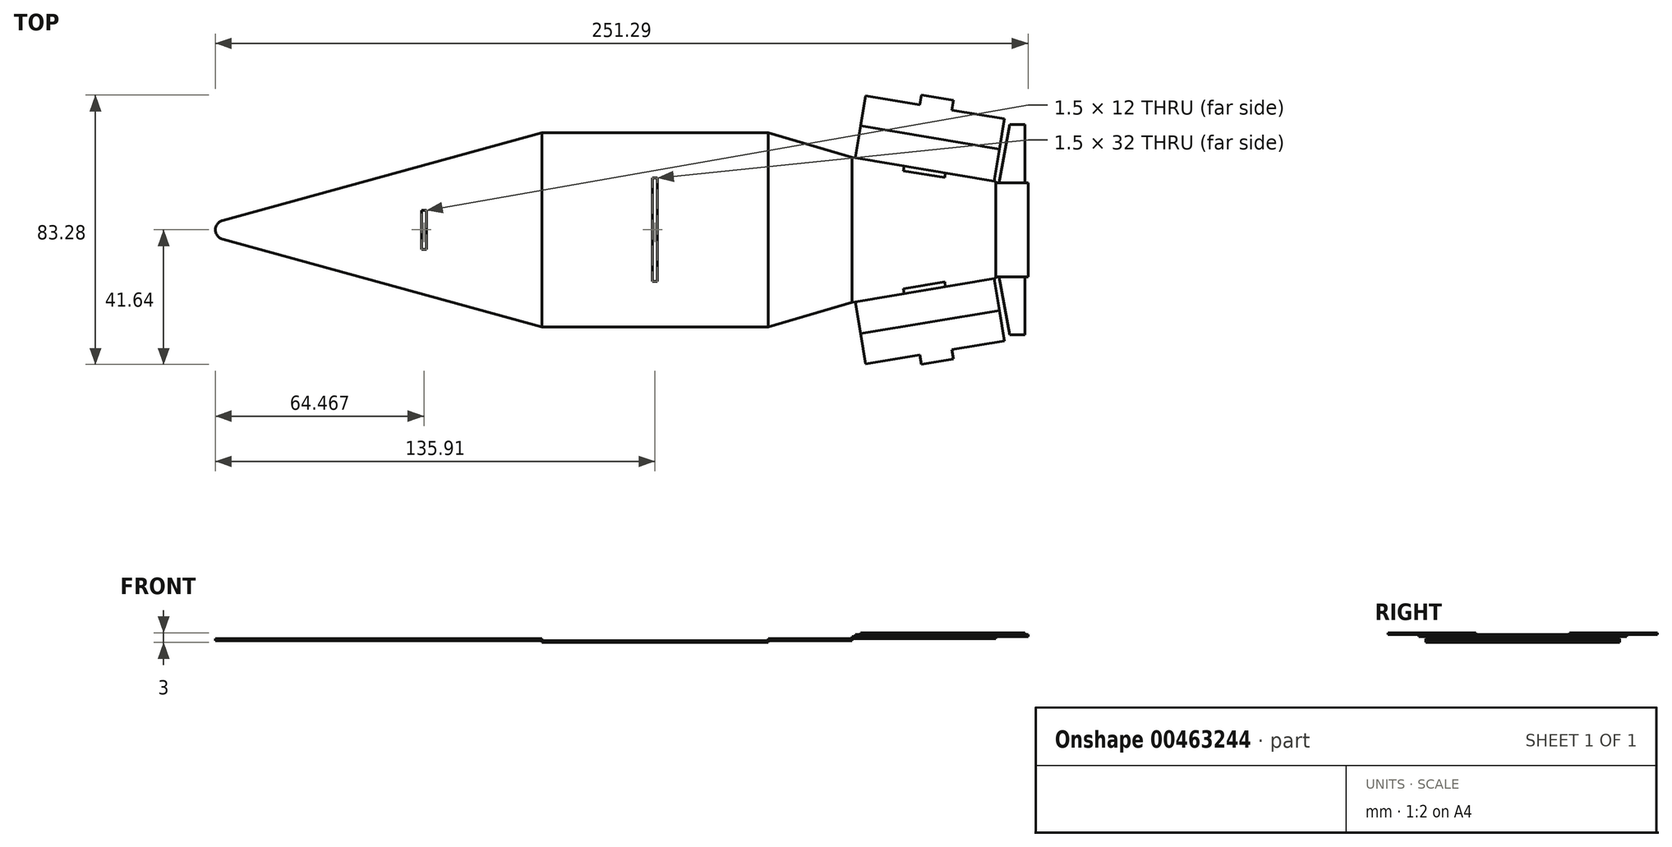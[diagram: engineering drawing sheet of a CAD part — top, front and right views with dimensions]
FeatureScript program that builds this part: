
annotation { "Feature Type Name" : "Feature", "Feature Type Description" : "" }
export const myFeature = defineFeature(function(context is Context, id is Id, definition is map)
    precondition{}
    {
        {
            var Q0;
            Q0=qCreatedBy(makeId("Top.planeOp"),FACE);
            var sketch = newSketch(context, id + "F0", { "sketchPlane" : qUnion([Q0])});
            skLineSegment(sketch, "E0.bottom", {"start": v(-35, 30) * mm, "end": v(35, 30) * mm});
            skLineSegment(sketch, "E0.top", {"start": v(-35, -30) * mm, "end": v(35, -30) * mm});
            skLineSegment(sketch, "E0.left", {"start": v(-35, 30) * mm, "end": v(-35, -30) * mm});
            skLineSegment(sketch, "E0.right", {"start": v(35, 30) * mm, "end": v(35, -30) * mm});
            skPoint(sketch, "E0.middle", {"position": v(0, 0) * mm});
            skLineSegment(sketch, "E1.0", {"start": v(-0.75, 16) * mm, "end": v(-0.75, -16) * mm});
            skLineSegment(sketch, "E2.0", {"start": v(0.75, 16) * mm, "end": v(0.75, -16) * mm});
            skLineSegment(sketch, "E3.0", {"start": v(-0.75, -16) * mm, "end": v(0.75, -16) * mm});
            skLineSegment(sketch, "E4.0", {"start": v(-0.75, 16) * mm, "end": v(0.75, 16) * mm});
            skSolve(sketch);
        }
        {
            var Q0;
            Q0 = qSketchRegion(id + "F0", true);
            extrude(context, id + "F1", {"entities" : qUnion([Q0]), "depth" : .6 * mm});
        }
        {
            var Q0;
            Q0=makeQuery(id+"F1.opExtrude","CAP_FACE",FACE,{"disambiguationData":[OSD([sQuery(id+"F0.wireOp",EDGE,"E0.bottom"),sQuery(id+"F0.wireOp",EDGE,"E0.top"),sQuery(id+"F0.wireOp",EDGE,"E0.left"),sQuery(id+"F0.wireOp",EDGE,"E0.right"),sQuery(id+"F0.wireOp",EDGE,"E1.0"),sQuery(id+"F0.wireOp",EDGE,"E2.0"),sQuery(id+"F0.wireOp",EDGE,"E3.0"),sQuery(id+"F0.wireOp",EDGE,"E4.0")])],"isStart":false});
            var sketch = newSketch(context, id + "F2", { "sketchPlane" : qUnion([Q0])});
            skLineSegment(sketch, "E5", {"start": v(-144.24, 0) * mm, "end": v(-35, 30) * mm});
            skLineSegment(sketch, "E6", {"start": v(-35, 30) * mm, "end": v(-35, -30) * mm});
            skLineSegment(sketch, "E7", {"start": v(-35, -30) * mm, "end": v(-144.24, 0) * mm});
            skLineSegment(sketch, "E8", {"start": v(-70.7, 6) * mm, "end": v(-70.7, -6) * mm});
            skLineSegment(sketch, "E9.0", {"start": v(-72.2, 6) * mm, "end": v(-72.2, -6) * mm});
            skLineSegment(sketch, "E10", {"start": v(-72.2, 6) * mm, "end": v(-70.7, 6) * mm});
            skLineSegment(sketch, "E11", {"start": v(-72.2, -6) * mm, "end": v(-70.7, -6) * mm});
            skSolve(sketch);
        }
        {
            var Q0;
            Q0 = qSketchRegion(id + "F2", true);
            extrude(context, id + "F3", {"entities" : qUnion([Q0]), "depth" : .6 * mm});
        }
        {
            var Q0;
            Q0=makeQuery(id+"F1.opExtrude","CAP_FACE",FACE,{"disambiguationData":[OSD([sQuery(id+"F0.wireOp",EDGE,"E0.bottom"),sQuery(id+"F0.wireOp",EDGE,"E0.top"),sQuery(id+"F0.wireOp",EDGE,"E0.left"),sQuery(id+"F0.wireOp",EDGE,"E0.right"),sQuery(id+"F0.wireOp",EDGE,"E1.0"),sQuery(id+"F0.wireOp",EDGE,"E2.0"),sQuery(id+"F0.wireOp",EDGE,"E3.0"),sQuery(id+"F0.wireOp",EDGE,"E4.0")])],"isStart":false});
            var sketch = newSketch(context, id + "F4", { "sketchPlane" : qUnion([Q0])});
            skLineSegment(sketch, "E12.0", {"start": v(35, 30) * mm, "end": v(35, -30) * mm});
            skLineSegment(sketch, "E13", {"start": v(35, 30) * mm, "end": v(60.94, 22.41) * mm});
            skLineSegment(sketch, "E14.MirrorCS", {"start": v(35, -30) * mm, "end": v(60.94, -22.41) * mm});
            skLineSegment(sketch, "E15", {"start": v(60.94, 22.41) * mm, "end": v(60.94, -22.41) * mm});
            skSolve(sketch);
        }
        {
            var Q0;
            Q0 = qSketchRegion(id + "F4", true);
            extrude(context, id + "F5", {"entities" : qUnion([Q0]), "depth" : .6 * mm});
        }
        {
            var Q0;
            Q0=makeQuery(id+"F5.opExtrude","CAP_FACE",FACE,{"disambiguationData":[OSD([sQuery(id+"F4.wireOp",EDGE,"E12.0"),sQuery(id+"F4.wireOp",EDGE,"E13"),sQuery(id+"F4.wireOp",EDGE,"E14.MirrorCS"),sQuery(id+"F4.wireOp",EDGE,"E15")])],"isStart":false});
            var sketch = newSketch(context, id + "F6", { "sketchPlane" : qUnion([Q0])});
            skLineSegment(sketch, "E16.0", {"start": v(60.94, 22.41) * mm, "end": v(60.94, -22.41) * mm});
            skLineSegment(sketch, "E17", {"start": v(60.94, 22.41) * mm, "end": v(105.38, 15) * mm});
            skPoint(sketch, "E18.endSnap0", {"position": v(60.94, 0) * mm});
            skLineSegment(sketch, "E19.MirrorCS", {"start": v(60.94, -22.41) * mm, "end": v(105.38, -15) * mm});
            skLineSegment(sketch, "E20", {"start": v(105.38, 15) * mm, "end": v(105.38, -15) * mm});
            skSolve(sketch);
        }
        {
            var Q0;
            Q0 = qSketchRegion(id + "F6", true);
            extrude(context, id + "F7", {"entities" : qUnion([Q0]), "depth" : .6 * mm});
        }
        {
            var Q0;
            Q0=makeQuery(id+"F7.opExtrude","CAP_FACE",FACE,{"disambiguationData":[OSD([sQuery(id+"F6.wireOp",EDGE,"E16.0"),sQuery(id+"F6.wireOp",EDGE,"E17"),sQuery(id+"F6.wireOp",EDGE,"E19.MirrorCS"),sQuery(id+"F6.wireOp",EDGE,"E20")])],"isStart":false});
            var sketch = newSketch(context, id + "F8", { "sketchPlane" : qUnion([Q0])});
            skLineSegment(sketch, "E21.0", {"start": v(61.93, -22.25) * mm, "end": v(105.38, -15) * mm});
            skLineSegment(sketch, "E22", {"start": v(105.38, -15) * mm, "end": v(107.02, -24.87) * mm});
            skLineSegment(sketch, "E23", {"start": v(63.57, -32.11) * mm, "end": v(107.02, -24.87) * mm});
            skLineSegment(sketch, "E24.0", {"start": v(61.93, -22.25) * mm, "end": v(63.57, -32.11) * mm});
            skPoint(sketch, "E25.orphan", {"position": v(60.94, -22.41) * mm});
            skPoint(sketch, "E26.endSnap0", {"position": v(105.38, 0) * mm});
            skLineSegment(sketch, "E27.MirrorCS", {"start": v(105.38, 15) * mm, "end": v(107.02, 24.87) * mm});
            skLineSegment(sketch, "E28.MirrorCS", {"start": v(61.93, 22.25) * mm, "end": v(105.38, 15) * mm});
            skLineSegment(sketch, "E29.MirrorCS", {"start": v(63.57, 32.11) * mm, "end": v(107.02, 24.87) * mm});
            skLineSegment(sketch, "E30.MirrorCS", {"start": v(61.93, 22.25) * mm, "end": v(63.57, 32.11) * mm});
            skPoint(sketch, "E31.MirrorP", {"position": v(60.94, 22.41) * mm});
            skLineSegment(sketch, "E32.0", {"start": v(105.38, 14.5) * mm, "end": v(105.38, -14.5) * mm});
            skLineSegment(sketch, "E33.0", {"start": v(115.38, 14.5) * mm, "end": v(115.38, -14.5) * mm});
            skLineSegment(sketch, "E34.0", {"start": v(105.38, 14.5) * mm, "end": v(115.38, 14.5) * mm});
            skLineSegment(sketch, "E35.0", {"start": v(105.38, -14.5) * mm, "end": v(115.38, -14.5) * mm});
            skPoint(sketch, "E36.orphan", {"position": v(105.38, 15) * mm});
            skSolve(sketch);
        }
        {
            var Q0;
            Q0 = qSketchRegion(id + "F8", true);
            extrude(context, id + "F9", {"entities" : qUnion([Q0]), "depth" : .6 * mm});
        }
        {
            var Q0;
            Q0=makeQuery(id+"F9.opExtrude","CAP_FACE",FACE,{"disambiguationData":[OSD([sQuery(id+"F8.wireOp",EDGE,"E21.0"),sQuery(id+"F8.wireOp",EDGE,"E22"),sQuery(id+"F8.wireOp",EDGE,"E23"),sQuery(id+"F8.wireOp",EDGE,"E24.0")])],"isStart":false});
            var sketch = newSketch(context, id + "F10", { "sketchPlane" : qUnion([Q0])});
            skLineSegment(sketch, "E37.0", {"start": v(63.57, -32.11) * mm, "end": v(107.02, -24.87) * mm});
            skLineSegment(sketch, "E38.0", {"start": v(65.14, -41.48) * mm, "end": v(81.93, -38.69) * mm});
            skLineSegment(sketch, "E39", {"start": v(63.57, -32.11) * mm, "end": v(65.14, -41.48) * mm});
            skLineSegment(sketch, "E40", {"start": v(107.02, -24.87) * mm, "end": v(108.59, -34.24) * mm});
            skLineSegment(sketch, "E41.0", {"start": v(82.42, -41.64) * mm, "end": v(92.29, -40) * mm});
            skLineSegment(sketch, "E42.0", {"start": v(92.29, -40) * mm, "end": v(91.8, -37.04) * mm});
            skLineSegment(sketch, "E43.0", {"start": v(82.42, -41.64) * mm, "end": v(81.93, -38.69) * mm});
            skLineSegment(sketch, "E44.trimOffspring", {"start": v(91.8, -37.04) * mm, "end": v(108.59, -34.24) * mm});
            skLineSegment(sketch, "E45.MirrorCS", {"start": v(92.29, 40) * mm, "end": v(91.8, 37.04) * mm});
            skLineSegment(sketch, "E46.MirrorCS", {"start": v(82.42, 41.64) * mm, "end": v(81.93, 38.69) * mm});
            skLineSegment(sketch, "E47.MirrorCS", {"start": v(63.57, 32.11) * mm, "end": v(107.02, 24.87) * mm});
            skLineSegment(sketch, "E48.MirrorCS", {"start": v(65.14, 41.48) * mm, "end": v(81.93, 38.69) * mm});
            skLineSegment(sketch, "E49.MirrorCS", {"start": v(91.8, 37.04) * mm, "end": v(108.59, 34.24) * mm});
            skLineSegment(sketch, "E50.MirrorCS", {"start": v(63.57, 32.11) * mm, "end": v(65.14, 41.48) * mm});
            skLineSegment(sketch, "E51.MirrorCS", {"start": v(82.42, 41.64) * mm, "end": v(92.29, 40) * mm});
            skLineSegment(sketch, "E52.MirrorCS", {"start": v(107.02, 24.87) * mm, "end": v(108.59, 34.24) * mm});
            skSolve(sketch);
        }
        {
            var Q0;
            Q0 = qSketchRegion(id + "F10", true);
            extrude(context, id + "F11", {"entities" : qUnion([Q0]), "depth" : .6 * mm});
        }
        {
            var Q0;
            Q0=makeQuery(id+"F11.opExtrude","CAP_FACE",FACE,{"disambiguationData":[OSD([sQuery(id+"F10.wireOp",EDGE,"E45.MirrorCS"),sQuery(id+"F10.wireOp",EDGE,"E46.MirrorCS"),sQuery(id+"F10.wireOp",EDGE,"E47.MirrorCS"),sQuery(id+"F10.wireOp",EDGE,"E48.MirrorCS"),sQuery(id+"F10.wireOp",EDGE,"E49.MirrorCS"),sQuery(id+"F10.wireOp",EDGE,"E50.MirrorCS"),sQuery(id+"F10.wireOp",EDGE,"E51.MirrorCS"),sQuery(id+"F10.wireOp",EDGE,"E52.MirrorCS")])],"isStart":false});
            var sketch = newSketch(context, id + "F12", { "sketchPlane" : qUnion([Q0])});
            skPoint(sketch, "E53.0", {"position": v(105.38, 15) * mm});
            skLineSegment(sketch, "E54.0", {"start": v(108.1, 34.32) * mm, "end": v(104.89, 15.09) * mm});
            skLineSegment(sketch, "E55", {"start": v(104.89, 15.09) * mm, "end": v(107, 14.74) * mm});
            skLineSegment(sketch, "E56", {"start": v(107, 14.74) * mm, "end": v(111.15, 36.88) * mm});
            skLineSegment(sketch, "E57", {"start": v(108.1, 34.32) * mm, "end": v(108.99, 36) * mm});
            skLineSegment(sketch, "E58", {"start": v(108.99, 36) * mm, "end": v(111.15, 36.88) * mm});
            skLineSegment(sketch, "E59.MirrorCS", {"start": v(104.89, -15.09) * mm, "end": v(107, -14.74) * mm});
            skLineSegment(sketch, "E60.MirrorCS", {"start": v(108.99, -36) * mm, "end": v(111.15, -36.88) * mm});
            skLineSegment(sketch, "E61.MirrorCS", {"start": v(108.1, -34.32) * mm, "end": v(108.99, -36) * mm});
            skLineSegment(sketch, "E62.MirrorCS", {"start": v(108.1, -34.32) * mm, "end": v(104.89, -15.09) * mm});
            skLineSegment(sketch, "E63.MirrorCS", {"start": v(107, -14.74) * mm, "end": v(111.15, -36.88) * mm});
            skPoint(sketch, "E64.MirrorP", {"position": v(105.38, -15) * mm});
            skSolve(sketch);
        }
        {
            var Q0;
            Q0 = qSketchRegion(id + "F12", true);
            extrude(context, id + "F13", {"entities" : qUnion([Q0]), "operationType" : NewBodyOperationType.REMOVE, "oppositeDirection" : true, "depth" : 25 * mm});
        }
        {
            var Q0;
            Q0=makeQuery(id+"F9.opExtrude","CAP_FACE",FACE,{"disambiguationData":[OSD([sQuery(id+"F8.wireOp",EDGE,"E32.0"),sQuery(id+"F8.wireOp",EDGE,"E33.0"),sQuery(id+"F8.wireOp",EDGE,"E34.0"),sQuery(id+"F8.wireOp",EDGE,"E35.0")])],"isStart":false});
            var sketch = newSketch(context, id + "F14", { "sketchPlane" : qUnion([Q0])});
            skLineSegment(sketch, "E65", {"start": v(106.38, 14.5) * mm, "end": v(114.38, 14.5) * mm});
            skLineSegment(sketch, "E66", {"start": v(114.38, 14.5) * mm, "end": v(114.38, 32.5) * mm});
            skLineSegment(sketch, "E67", {"start": v(106.38, 14.5) * mm, "end": v(109.73, 32.5) * mm});
            skLineSegment(sketch, "E68", {"start": v(109.73, 32.5) * mm, "end": v(114.38, 32.5) * mm});
            skLineSegment(sketch, "E69.MirrorCS", {"start": v(109.73, -32.5) * mm, "end": v(114.38, -32.5) * mm});
            skLineSegment(sketch, "E70.MirrorCS", {"start": v(106.38, -14.5) * mm, "end": v(114.38, -14.5) * mm});
            skLineSegment(sketch, "E71.MirrorCS", {"start": v(114.38, -14.5) * mm, "end": v(114.38, -32.5) * mm});
            skLineSegment(sketch, "E72.MirrorCS", {"start": v(106.38, -14.5) * mm, "end": v(109.73, -32.5) * mm});
            skSolve(sketch);
        }
        {
            var Q0;
            Q0 = qSketchRegion(id + "F14", true);
            extrude(context, id + "F15", {"entities" : qUnion([Q0]), "depth" : .6 * mm});
        }
        {
            var Q0;
            Q0=makeQuery(id+"F7.opExtrude","CAP_FACE",FACE,{"disambiguationData":[OSD([sQuery(id+"F6.wireOp",EDGE,"E16.0"),sQuery(id+"F6.wireOp",EDGE,"E17"),sQuery(id+"F6.wireOp",EDGE,"E19.MirrorCS"),sQuery(id+"F6.wireOp",EDGE,"E20")])],"isStart":false});
            var sketch = newSketch(context, id + "F16", { "sketchPlane" : qUnion([Q0])});
            skLineSegment(sketch, "E73.0", {"start": v(77, -19.74) * mm, "end": v(89.82, -17.6) * mm});
            skLineSegment(sketch, "E74.0", {"start": v(76.75, -18.26) * mm, "end": v(89.57, -16.12) * mm});
            skLineSegment(sketch, "E75.0", {"start": v(76.75, -18.26) * mm, "end": v(77, -19.74) * mm});
            skLineSegment(sketch, "E76.0", {"start": v(89.57, -16.12) * mm, "end": v(89.82, -17.6) * mm});
            skPoint(sketch, "E77.orphan", {"position": v(61.68, -20.77) * mm});
            skPoint(sketch, "E78.orphan", {"position": v(61.93, -22.25) * mm});
            skPoint(sketch, "E79.orphan", {"position": v(104.64, -13.61) * mm});
            skPoint(sketch, "E80.orphan", {"position": v(104.89, -15.09) * mm});
            skPoint(sketch, "E81.end.orphan", {"position": v(83.4, -18.67) * mm});
            skPoint(sketch, "E81.start.orphan", {"position": v(83.16, -17.19) * mm});
            skLineSegment(sketch, "E82.MirrorCS", {"start": v(76.75, 18.26) * mm, "end": v(77, 19.74) * mm});
            skLineSegment(sketch, "E83.MirrorCS", {"start": v(89.57, 16.12) * mm, "end": v(89.82, 17.6) * mm});
            skPoint(sketch, "E84.MirrorP", {"position": v(104.89, 15.09) * mm});
            skPoint(sketch, "E85.MirrorP", {"position": v(83.4, 18.67) * mm});
            skPoint(sketch, "E86.MirrorP", {"position": v(83.16, 17.19) * mm});
            skLineSegment(sketch, "E87.MirrorCS", {"start": v(76.75, 18.26) * mm, "end": v(89.57, 16.12) * mm});
            skLineSegment(sketch, "E88.MirrorCS", {"start": v(77, 19.74) * mm, "end": v(89.82, 17.6) * mm});
            skSolve(sketch);
        }
        {
            var Q0;
            Q0 = qSketchRegion(id + "F16", true);
            extrude(context, id + "F17", {"entities" : qUnion([Q0]), "operationType" : NewBodyOperationType.REMOVE, "oppositeDirection" : true, "depth" : 25 * mm});
        }
        {
            var Q0;
            Q0=makeQuery(id+"F3.opExtrude","SWEPT_EDGE",EDGE,{"disambiguationData":[OSD([sQuery(id+"F2.wireOp",EDGE,"E5"),sQuery(id+"F2.wireOp",EDGE,"E7")])]});
            fillet(context, id + "F18", {"entities" : qUnion([Q0]), "radius" : 3 * mm, "tangentPropagation" : true, "allowEdgeOverflow" : false});
        }
    });
